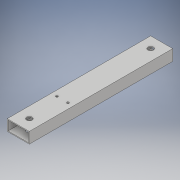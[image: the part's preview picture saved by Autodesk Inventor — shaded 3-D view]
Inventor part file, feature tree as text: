
AUTODESK INVENTOR PART (.ipt)
format: ipt  version: 2018 (Build 220112000, 112)  size: 123,904 bytes
history: native  units: in
note: dims shown in document units (in); Inventor stores cm internally (conversion verified against a paired STEP export)
features: extrude x2, sketch x2
ambient origin geometry x8: Origin, YZ Plane, XZ Plane, XY Plane, X Axis, Y Axis, Z Axis, Center Point
bodies: Solid1 (feature_tree)
feature tree (4):
  extrude  "Extrusion1"  Depth=1.0in
  extrude  "Extrusion2"  Depth=13.0in TaperAngle=0.0deg
  sketch  "Sketch1"  dims[d0=2.0in d1=1.0in]
  sketch  "Sketch2"  dims[d2=0.075in d3=13.0in d4=0.0in d5=1.0in d6=3.0in d7=1.0in d8=0.5in d9=0.5in d10=0.5in d11=0.5in d12=0.2031in d13=0.2031in d14=14.0in d15=0.0in]
